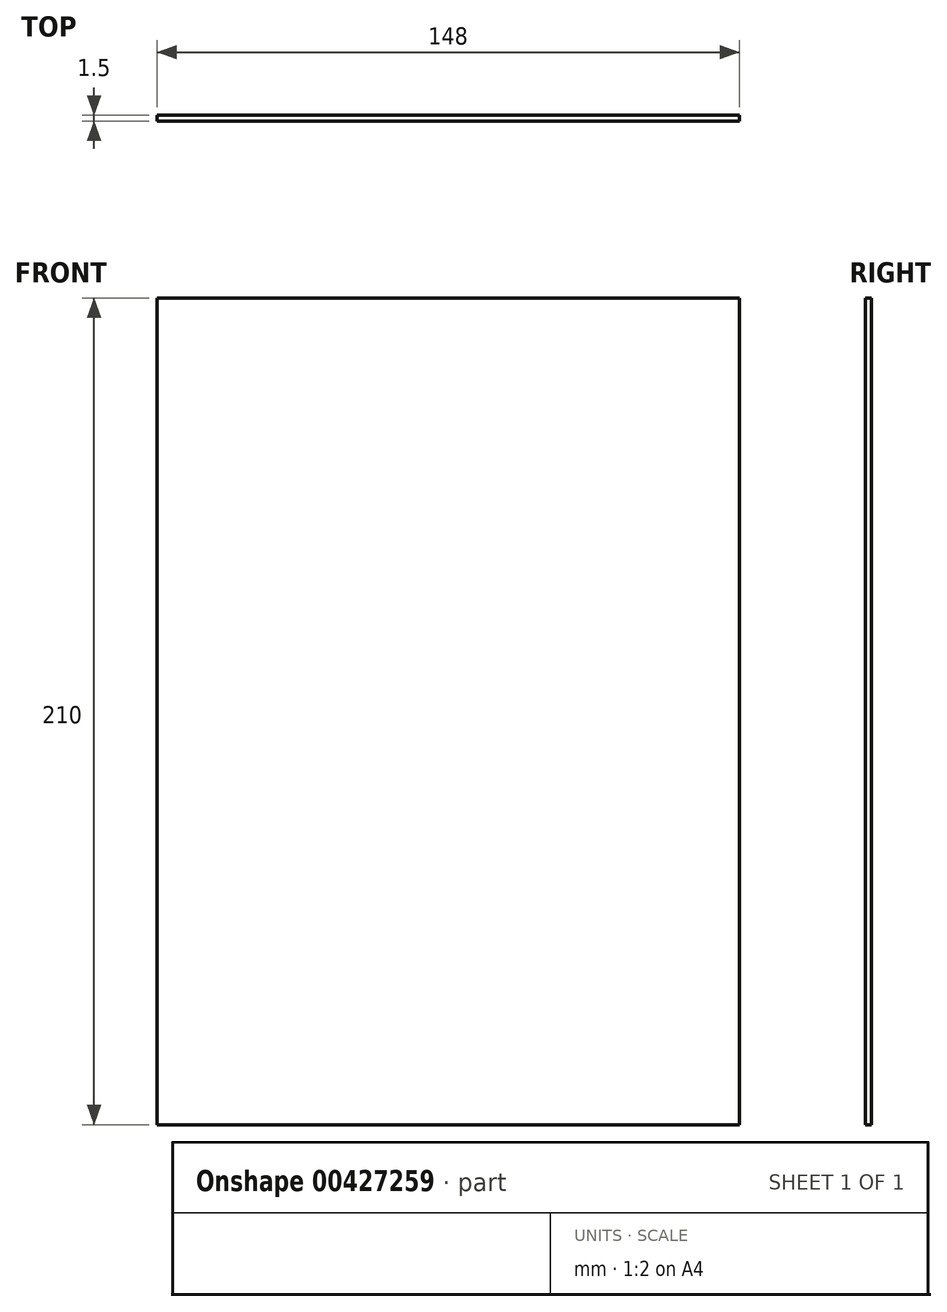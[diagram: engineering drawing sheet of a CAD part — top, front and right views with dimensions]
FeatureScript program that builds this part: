
annotation { "Feature Type Name" : "Feature", "Feature Type Description" : "" }
export const myFeature = defineFeature(function(context is Context, id is Id, definition is map)
    precondition{}
    {
        {
            var Q0;
            Q0=qCreatedBy(makeId("Front.planeOp"),FACE);
            var sketch = newSketch(context, id + "F0", { "sketchPlane" : qUnion([Q0])});
            skLineSegment(sketch, "E0", {"start": v(-158, 105) * mm, "end": v(-10, 105) * mm});
            skLineSegment(sketch, "E1", {"start": v(-10, 105) * mm, "end": v(-10, -105) * mm});
            skLineSegment(sketch, "E2", {"start": v(-10, -105) * mm, "end": v(-158, -105) * mm});
            skLineSegment(sketch, "E3", {"start": v(-158, 105) * mm, "end": v(-158, -105) * mm});
            skSolve(sketch);
        }
        {
            var Q0;
            Q0=makeQuery(id+"F0.imprint","IMPRINT",FACE,{"disambiguationData":[TD([[makeQuery(id+"F0.imprint","IMPRINT",EDGE,{"derivedFrom":sQuery(id+"F0.wireOp",EDGE,"E0")}),-1.0]])]});
            extrude(context, id + "F1", {"entities" : qUnion([Q0]), "depth" : 1.5 * mm});
        }
    });
